# Revit family: Single Handle Lavatory Faucet with pop-up waste_TOTO_TLG10305
name_source: partatom
category: 衛生器具
revit_build: Autodesk Revit 2018 (Build: 20170223_1515(x64)
units: mm (PartAtom-declared; Revit-internal decimal feet)

## family parameters
OmniClass タイトル = Sanitary, Laundry, and Cleaning Equipment
OmniClass 番号 = 23.45.00.00
パーツ タイプ = 標準
ロード時にボイドで切り取り = いいえ
丸型コネクタ寸法 = 直径を使用
作業面ベース = いいえ
共有 = いいえ
常に垂直 = はい
部屋計算ポイント = いいえ

## types (1)
- Single Handle Lavatory Faucet with pop-up waste_TOTO_TLG10305
    Chrome = Chrome
    Height = 328
    Length = 209
    TOTO asiaoceania = TLG10305V
    TOTO china = TLG10305B
    TOTO hongkong = TLG10305H
    TOTO india = TLG10305B
    TOTO korea = TLG10305K
    TOTO thailand = TLG10305T
    TOTO usa = TLG10305U
    TOTO vietnam = TLG10305V
    Width = 48  [stored 0.15748 ft]
    製造元 = TOTO LTD.
    説明 = Single Handle Lavatory Faucet with pop-up waste

note: [stored X ft] marks values corroborated as IEEE doubles in the binary element streams (Revit-internal decimal feet)
